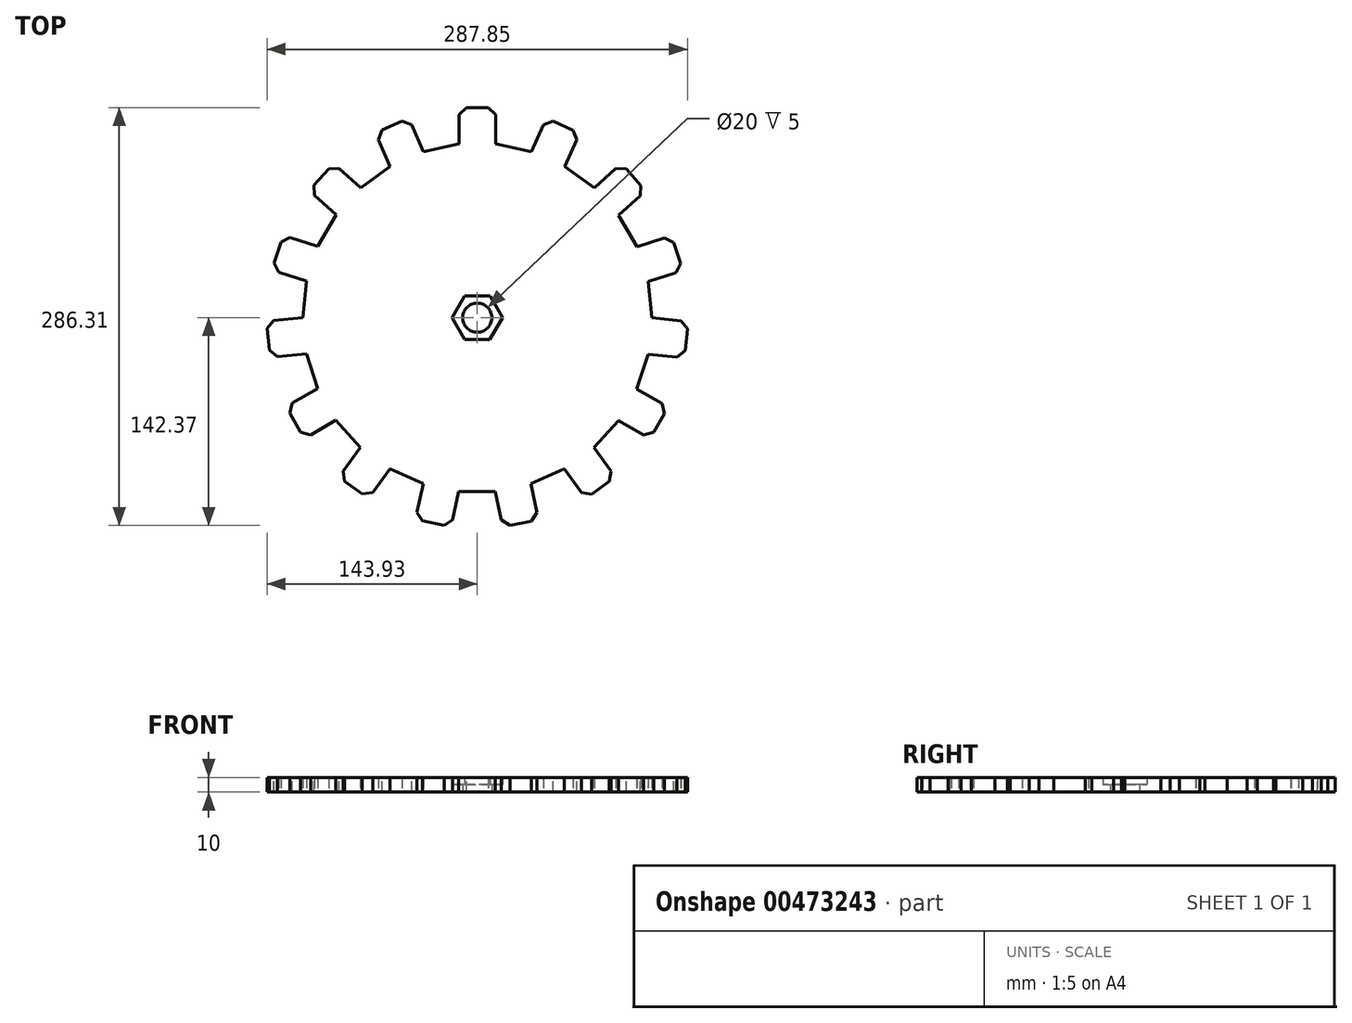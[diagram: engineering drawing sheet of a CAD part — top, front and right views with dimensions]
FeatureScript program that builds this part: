
annotation { "Feature Type Name" : "Feature", "Feature Type Description" : "" }
export const myFeature = defineFeature(function(context is Context, id is Id, definition is map)
    precondition{}
    {
        {
            var Q0;
            Q0=qCreatedBy(makeId("Top.planeOp"),FACE);
            var sketch = newSketch(context, id + "F0", { "sketchPlane" : qUnion([Q0])});
            skCircle(sketch, "E0.cCircle", {"center": v(0, 0) * mm, "radius": 118.93 * mm, "construction": true});
            skLineSegment(sketch, "E0.0", {"start": v(-109.2, 48.75) * mm, "end": v(-96.68, 70.39) * mm});
            skLineSegment(sketch, "E0.1", {"start": v(-96.68, 70.39) * mm, "end": v(-79.93, 88.95) * mm});
            skLineSegment(sketch, "E0.2", {"start": v(-79.93, 88.95) * mm, "end": v(-59.69, 103.62) * mm});
            skLineSegment(sketch, "E0.3", {"start": v(-59.69, 103.62) * mm, "end": v(-36.84, 113.77) * mm});
            skLineSegment(sketch, "E0.4", {"start": v(-36.84, 113.77) * mm, "end": v(-12.38, 118.94) * mm});
            skLineSegment(sketch, "E0.5", {"start": v(-12.38, 118.94) * mm, "end": v(12.62, 118.92) * mm});
            skLineSegment(sketch, "E0.6", {"start": v(12.62, 118.92) * mm, "end": v(37.07, 113.7) * mm});
            skLineSegment(sketch, "E0.7", {"start": v(37.07, 113.7) * mm, "end": v(59.9, 103.5) * mm});
            skLineSegment(sketch, "E0.8", {"start": v(59.9, 103.5) * mm, "end": v(80.1, 88.79) * mm});
            skLineSegment(sketch, "E0.9", {"start": v(80.1, 88.79) * mm, "end": v(96.82, 70.2) * mm});
            skLineSegment(sketch, "E0.10", {"start": v(96.82, 70.2) * mm, "end": v(109.3, 48.53) * mm});
            skLineSegment(sketch, "E0.11", {"start": v(109.3, 48.53) * mm, "end": v(117, 24.74) * mm});
            skLineSegment(sketch, "E0.12", {"start": v(117, 24.74) * mm, "end": v(119.58, -0.12) * mm});
            skLineSegment(sketch, "E0.13", {"start": v(119.58, -0.12) * mm, "end": v(116.95, -24.98) * mm});
            skLineSegment(sketch, "E0.14", {"start": v(116.95, -24.98) * mm, "end": v(109.2, -48.75) * mm});
            skLineSegment(sketch, "E0.15", {"start": v(109.2, -48.75) * mm, "end": v(96.68, -70.39) * mm});
            skLineSegment(sketch, "E0.16", {"start": v(96.68, -70.39) * mm, "end": v(79.93, -88.95) * mm});
            skLineSegment(sketch, "E0.17", {"start": v(79.93, -88.95) * mm, "end": v(59.69, -103.62) * mm});
            skLineSegment(sketch, "E0.18", {"start": v(59.69, -103.62) * mm, "end": v(36.84, -113.77) * mm});
            skLineSegment(sketch, "E0.19", {"start": v(36.84, -113.77) * mm, "end": v(12.38, -118.94) * mm});
            skLineSegment(sketch, "E0.20", {"start": v(12.38, -118.94) * mm, "end": v(-12.62, -118.92) * mm});
            skLineSegment(sketch, "E0.21", {"start": v(-12.62, -118.92) * mm, "end": v(-37.07, -113.7) * mm});
            skLineSegment(sketch, "E0.22", {"start": v(-37.07, -113.7) * mm, "end": v(-59.9, -103.5) * mm});
            skLineSegment(sketch, "E0.23", {"start": v(-59.9, -103.5) * mm, "end": v(-80.1, -88.79) * mm});
            skLineSegment(sketch, "E0.24", {"start": v(-80.1, -88.79) * mm, "end": v(-96.82, -70.2) * mm});
            skLineSegment(sketch, "E0.25", {"start": v(-96.82, -70.2) * mm, "end": v(-109.3, -48.53) * mm});
            skLineSegment(sketch, "E0.26", {"start": v(-109.3, -48.53) * mm, "end": v(-117, -24.74) * mm});
            skLineSegment(sketch, "E0.27", {"start": v(-117, -24.74) * mm, "end": v(-119.58, 0.12) * mm});
            skLineSegment(sketch, "E0.28", {"start": v(-119.58, 0.12) * mm, "end": v(-116.95, 24.98) * mm});
            skLineSegment(sketch, "E0.29", {"start": v(-116.95, 24.98) * mm, "end": v(-109.2, 48.75) * mm});
            skPoint(sketch, "E0.0.midPoint", {"position": v(-102.94, 59.57) * mm});
            skCircle(sketch, "E1.cCircle", {"center": v(0, 0) * mm, "radius": 15 * mm, "construction": true});
            skLineSegment(sketch, "E1.0", {"start": v(-17.32, 0.02) * mm, "end": v(-8.65, 15) * mm});
            skLineSegment(sketch, "E1.1", {"start": v(-8.65, 15) * mm, "end": v(8.68, 15) * mm});
            skLineSegment(sketch, "E1.2", {"start": v(8.68, 15) * mm, "end": v(17.32, -0.02) * mm});
            skLineSegment(sketch, "E1.3", {"start": v(17.32, -0.02) * mm, "end": v(8.65, -15) * mm});
            skLineSegment(sketch, "E1.4", {"start": v(8.65, -15) * mm, "end": v(-8.68, -15) * mm});
            skLineSegment(sketch, "E1.5", {"start": v(-8.68, -15) * mm, "end": v(-17.32, 0.02) * mm});
            skPoint(sketch, "E1.0.midPoint", {"position": v(-12.98, 7.51) * mm});
            skCircle(sketch, "E2", {"center": v(0, 0) * mm, "radius": 10 * mm});
            skSolve(sketch);
        }
        {
            var Q0;
            Q0 = qSketchRegion(id + "F0", true);
            extrude(context, id + "F1", {"entities" : qUnion([Q0]), "depth" : 10 * mm});
        }
        {
            var Q0;
            Q0=makeQuery(id+"F1.opExtrude","SWEPT_FACE",FACE,{"disambiguationData":[OSD([sQuery(id+"F0.wireOp",EDGE,"E0.5")])]});
            extrude(context, id + "F2", {"entities" : qUnion([Q0]), "operationType" : NewBodyOperationType.ADD, "depth" : 25 * mm});
        }
        {
            var Q0;
            Q0=makeQuery(id+"F1.opExtrude","SWEPT_FACE",FACE,{"disambiguationData":[OSD([sQuery(id+"F0.wireOp",EDGE,"E0.3")])]});
            extrude(context, id + "F3", {"entities" : qUnion([Q0]), "operationType" : NewBodyOperationType.ADD, "depth" : 25 * mm});
        }
        {
            var Q0;
            Q0=makeQuery(id+"F1.opExtrude","SWEPT_FACE",FACE,{"disambiguationData":[OSD([sQuery(id+"F0.wireOp",EDGE,"E0.1")])]});
            extrude(context, id + "F4", {"entities" : qUnion([Q0]), "operationType" : NewBodyOperationType.ADD, "depth" : 25 * mm});
        }
        {
            var Q0;
            Q0=makeQuery(id+"F1.opExtrude","SWEPT_FACE",FACE,{"disambiguationData":[OSD([sQuery(id+"F0.wireOp",EDGE,"E0.29")])]});
            extrude(context, id + "F5", {"entities" : qUnion([Q0]), "operationType" : NewBodyOperationType.ADD, "depth" : 25 * mm});
        }
        {
            var Q0;
            Q0=makeQuery(id+"F1.opExtrude","SWEPT_FACE",FACE,{"disambiguationData":[OSD([sQuery(id+"F0.wireOp",EDGE,"E0.27")])]});
            extrude(context, id + "F6", {"entities" : qUnion([Q0]), "operationType" : NewBodyOperationType.ADD, "depth" : 25 * mm});
        }
        {
            var Q0;
            Q0=makeQuery(id+"F1.opExtrude","SWEPT_FACE",FACE,{"disambiguationData":[OSD([sQuery(id+"F0.wireOp",EDGE,"E0.7")])]});
            extrude(context, id + "F7", {"entities" : qUnion([Q0]), "operationType" : NewBodyOperationType.ADD, "depth" : 25 * mm});
        }
        {
            var Q0;
            Q0=makeQuery(id+"F1.opExtrude","SWEPT_FACE",FACE,{"disambiguationData":[OSD([sQuery(id+"F0.wireOp",EDGE,"E0.9")])]});
            extrude(context, id + "F8", {"entities" : qUnion([Q0]), "operationType" : NewBodyOperationType.ADD, "depth" : 25 * mm});
        }
        {
            var Q0;
            Q0=makeQuery(id+"F1.opExtrude","SWEPT_FACE",FACE,{"disambiguationData":[OSD([sQuery(id+"F0.wireOp",EDGE,"E0.11")])]});
            extrude(context, id + "F9", {"entities" : qUnion([Q0]), "operationType" : NewBodyOperationType.ADD, "depth" : 25 * mm});
        }
        {
            var Q0;
            Q0=makeQuery(id+"F1.opExtrude","SWEPT_FACE",FACE,{"disambiguationData":[OSD([sQuery(id+"F0.wireOp",EDGE,"E0.13")])]});
            extrude(context, id + "F10", {"entities" : qUnion([Q0]), "operationType" : NewBodyOperationType.ADD, "depth" : 25 * mm});
        }
        {
            var Q0;
            Q0=makeQuery(id+"F1.opExtrude","SWEPT_FACE",FACE,{"disambiguationData":[OSD([sQuery(id+"F0.wireOp",EDGE,"E0.15")])]});
            extrude(context, id + "F11", {"entities" : qUnion([Q0]), "operationType" : NewBodyOperationType.ADD, "depth" : 25 * mm});
        }
        {
            var Q0;
            Q0=makeQuery(id+"F1.opExtrude","SWEPT_FACE",FACE,{"disambiguationData":[OSD([sQuery(id+"F0.wireOp",EDGE,"E0.17")])]});
            extrude(context, id + "F12", {"entities" : qUnion([Q0]), "operationType" : NewBodyOperationType.ADD, "depth" : 25 * mm});
        }
        {
            var Q0;
            Q0=makeQuery(id+"F1.opExtrude","SWEPT_FACE",FACE,{"disambiguationData":[OSD([sQuery(id+"F0.wireOp",EDGE,"E0.19")])]});
            extrude(context, id + "F13", {"entities" : qUnion([Q0]), "operationType" : NewBodyOperationType.ADD, "depth" : 25 * mm});
        }
        {
            var Q0;
            Q0=makeQuery(id+"F1.opExtrude","SWEPT_FACE",FACE,{"disambiguationData":[OSD([sQuery(id+"F0.wireOp",EDGE,"E0.21")])]});
            extrude(context, id + "F14", {"entities" : qUnion([Q0]), "operationType" : NewBodyOperationType.ADD, "depth" : 25 * mm});
        }
        {
            var Q0;
            Q0=makeQuery(id+"F1.opExtrude","SWEPT_FACE",FACE,{"disambiguationData":[OSD([sQuery(id+"F0.wireOp",EDGE,"E0.23")])]});
            extrude(context, id + "F15", {"entities" : qUnion([Q0]), "operationType" : NewBodyOperationType.ADD, "depth" : 25 * mm});
        }
        {
            var Q0;
            Q0=makeQuery(id+"F1.opExtrude","SWEPT_FACE",FACE,{"disambiguationData":[OSD([sQuery(id+"F0.wireOp",EDGE,"E0.25")])]});
            extrude(context, id + "F16", {"entities" : qUnion([Q0]), "operationType" : NewBodyOperationType.ADD, "depth" : 25 * mm});
        }
        {
            var Q0;
            Q0=makeQuery(id+"F10.opExtrude","CAP_EDGE",EDGE,{"disambiguationData":[OSD([sQuery(id+"F0.wireOp",EDGE,"E0.12"),sQuery(id+"F0.wireOp",EDGE,"E0.13")])],"isStart":false});
            var Q1;
            Q1=makeQuery(id+"F10.opExtrude","CAP_EDGE",EDGE,{"disambiguationData":[OSD([sQuery(id+"F0.wireOp",EDGE,"E0.13"),sQuery(id+"F0.wireOp",EDGE,"E0.14")])],"isStart":false});
            var Q2;
            Q2=makeQuery(id+"F9.opExtrude","CAP_EDGE",EDGE,{"disambiguationData":[OSD([sQuery(id+"F0.wireOp",EDGE,"E0.11"),sQuery(id+"F0.wireOp",EDGE,"E0.12")])],"isStart":false});
            var Q3;
            Q3=makeQuery(id+"F9.opExtrude","CAP_EDGE",EDGE,{"disambiguationData":[OSD([sQuery(id+"F0.wireOp",EDGE,"E0.10"),sQuery(id+"F0.wireOp",EDGE,"E0.11")])],"isStart":false});
            var Q4;
            Q4=makeQuery(id+"F8.opExtrude","CAP_EDGE",EDGE,{"disambiguationData":[OSD([sQuery(id+"F0.wireOp",EDGE,"E0.9"),sQuery(id+"F0.wireOp",EDGE,"E0.10")])],"isStart":false});
            var Q5;
            Q5=makeQuery(id+"F8.opExtrude","CAP_EDGE",EDGE,{"disambiguationData":[OSD([sQuery(id+"F0.wireOp",EDGE,"E0.8"),sQuery(id+"F0.wireOp",EDGE,"E0.9")])],"isStart":false});
            var Q6;
            Q6=makeQuery(id+"F7.opExtrude","CAP_EDGE",EDGE,{"disambiguationData":[OSD([sQuery(id+"F0.wireOp",EDGE,"E0.7"),sQuery(id+"F0.wireOp",EDGE,"E0.8")])],"isStart":false});
            var Q7;
            Q7=makeQuery(id+"F7.opExtrude","CAP_EDGE",EDGE,{"disambiguationData":[OSD([sQuery(id+"F0.wireOp",EDGE,"E0.6"),sQuery(id+"F0.wireOp",EDGE,"E0.7")])],"isStart":false});
            var Q8;
            Q8=makeQuery(id+"F2.opExtrude","CAP_EDGE",EDGE,{"disambiguationData":[OSD([sQuery(id+"F0.wireOp",EDGE,"E0.5"),sQuery(id+"F0.wireOp",EDGE,"E0.6")])],"isStart":false});
            var Q9;
            Q9=makeQuery(id+"F2.opExtrude","CAP_EDGE",EDGE,{"disambiguationData":[OSD([sQuery(id+"F0.wireOp",EDGE,"E0.4"),sQuery(id+"F0.wireOp",EDGE,"E0.5")])],"isStart":false});
            var Q10;
            Q10=makeQuery(id+"F3.opExtrude","CAP_EDGE",EDGE,{"disambiguationData":[OSD([sQuery(id+"F0.wireOp",EDGE,"E0.3"),sQuery(id+"F0.wireOp",EDGE,"E0.4")])],"isStart":false});
            var Q11;
            Q11=makeQuery(id+"F3.opExtrude","CAP_EDGE",EDGE,{"disambiguationData":[OSD([sQuery(id+"F0.wireOp",EDGE,"E0.2"),sQuery(id+"F0.wireOp",EDGE,"E0.3")])],"isStart":false});
            var Q12;
            Q12=makeQuery(id+"F13.opExtrude","CAP_EDGE",EDGE,{"disambiguationData":[OSD([sQuery(id+"F0.wireOp",EDGE,"E0.18"),sQuery(id+"F0.wireOp",EDGE,"E0.19")])],"isStart":false});
            var Q13;
            Q13=makeQuery(id+"F13.opExtrude","CAP_EDGE",EDGE,{"disambiguationData":[OSD([sQuery(id+"F0.wireOp",EDGE,"E0.19"),sQuery(id+"F0.wireOp",EDGE,"E0.20")])],"isStart":false});
            var Q14;
            Q14=makeQuery(id+"F12.opExtrude","CAP_EDGE",EDGE,{"disambiguationData":[OSD([sQuery(id+"F0.wireOp",EDGE,"E0.17"),sQuery(id+"F0.wireOp",EDGE,"E0.18")])],"isStart":false});
            var Q15;
            Q15=makeQuery(id+"F12.opExtrude","CAP_EDGE",EDGE,{"disambiguationData":[OSD([sQuery(id+"F0.wireOp",EDGE,"E0.16"),sQuery(id+"F0.wireOp",EDGE,"E0.17")])],"isStart":false});
            var Q16;
            Q16=makeQuery(id+"F4.opExtrude","CAP_EDGE",EDGE,{"disambiguationData":[OSD([sQuery(id+"F0.wireOp",EDGE,"E0.1"),sQuery(id+"F0.wireOp",EDGE,"E0.2")])],"isStart":false});
            var Q17;
            Q17=makeQuery(id+"F15.opExtrude","CAP_EDGE",EDGE,{"disambiguationData":[OSD([sQuery(id+"F0.wireOp",EDGE,"E0.22"),sQuery(id+"F0.wireOp",EDGE,"E0.23")])],"isStart":false});
            var Q18;
            Q18=makeQuery(id+"F14.opExtrude","CAP_EDGE",EDGE,{"disambiguationData":[OSD([sQuery(id+"F0.wireOp",EDGE,"E0.20"),sQuery(id+"F0.wireOp",EDGE,"E0.21")])],"isStart":false});
            var Q19;
            Q19=makeQuery(id+"F14.opExtrude","CAP_EDGE",EDGE,{"disambiguationData":[OSD([sQuery(id+"F0.wireOp",EDGE,"E0.21"),sQuery(id+"F0.wireOp",EDGE,"E0.22")])],"isStart":false});
            var Q20;
            Q20=makeQuery(id+"F16.opExtrude","CAP_EDGE",EDGE,{"disambiguationData":[OSD([sQuery(id+"F0.wireOp",EDGE,"E0.24"),sQuery(id+"F0.wireOp",EDGE,"E0.25")])],"isStart":false});
            var Q21;
            Q21=makeQuery(id+"F6.opExtrude","CAP_EDGE",EDGE,{"disambiguationData":[OSD([sQuery(id+"F0.wireOp",EDGE,"E0.26"),sQuery(id+"F0.wireOp",EDGE,"E0.27")])],"isStart":false});
            var Q22;
            Q22=makeQuery(id+"F5.opExtrude","CAP_EDGE",EDGE,{"disambiguationData":[OSD([sQuery(id+"F0.wireOp",EDGE,"E0.28"),sQuery(id+"F0.wireOp",EDGE,"E0.29")])],"isStart":false});
            var Q23;
            Q23=makeQuery(id+"F6.opExtrude","CAP_EDGE",EDGE,{"disambiguationData":[OSD([sQuery(id+"F0.wireOp",EDGE,"E0.27"),sQuery(id+"F0.wireOp",EDGE,"E0.28")])],"isStart":false});
            var Q24;
            Q24=makeQuery(id+"F16.opExtrude","CAP_EDGE",EDGE,{"disambiguationData":[OSD([sQuery(id+"F0.wireOp",EDGE,"E0.25"),sQuery(id+"F0.wireOp",EDGE,"E0.26")])],"isStart":false});
            var Q25;
            Q25=makeQuery(id+"F5.opExtrude","CAP_EDGE",EDGE,{"disambiguationData":[OSD([sQuery(id+"F0.wireOp",EDGE,"E0.0"),sQuery(id+"F0.wireOp",EDGE,"E0.29")])],"isStart":false});
            var Q26;
            Q26=makeQuery(id+"F4.opExtrude","CAP_EDGE",EDGE,{"disambiguationData":[OSD([sQuery(id+"F0.wireOp",EDGE,"E0.0"),sQuery(id+"F0.wireOp",EDGE,"E0.1")])],"isStart":false});
            var Q27;
            Q27=makeQuery(id+"F11.opExtrude","CAP_EDGE",EDGE,{"disambiguationData":[OSD([sQuery(id+"F0.wireOp",EDGE,"E0.14"),sQuery(id+"F0.wireOp",EDGE,"E0.15")])],"isStart":false});
            var Q28;
            Q28=makeQuery(id+"F11.opExtrude","CAP_EDGE",EDGE,{"disambiguationData":[OSD([sQuery(id+"F0.wireOp",EDGE,"E0.15"),sQuery(id+"F0.wireOp",EDGE,"E0.16")])],"isStart":false});
            var Q29;
            Q29=makeQuery(id+"F15.opExtrude","CAP_EDGE",EDGE,{"disambiguationData":[OSD([sQuery(id+"F0.wireOp",EDGE,"E0.23"),sQuery(id+"F0.wireOp",EDGE,"E0.24")])],"isStart":false});
            chamfer(context, id + "F17", {"entities" : qUnion([Q0, Q1, Q2, Q3, Q4, Q5, Q6, Q7, Q8, Q9, Q10, Q11, Q12, Q13, Q14, Q15, Q16, Q17, Q18, Q19, Q20, Q21, Q22, Q23, Q24, Q25, Q26, Q27, Q28, Q29]), "width" : 5 * mm, "tangentPropagation" : true});
        }
        {
            var Q0;
            Q0 = qSketchRegion(id + "F0", true);
            var Q1;
            Q1=makeQuery(id+"F0.imprint","IMPRINT",FACE,{"disambiguationData":[TD([[makeQuery(id+"F0.imprint","IMPRINT",EDGE,{"derivedFrom":sQuery(id+"F0.wireOp",EDGE,"E1.0")}),-1.0]])]});
            extrude(context, id + "F18", {"entities" : qUnion([Q0, Q1]), "operationType" : NewBodyOperationType.ADD, "depth" : 5 * mm});
        }
    });
